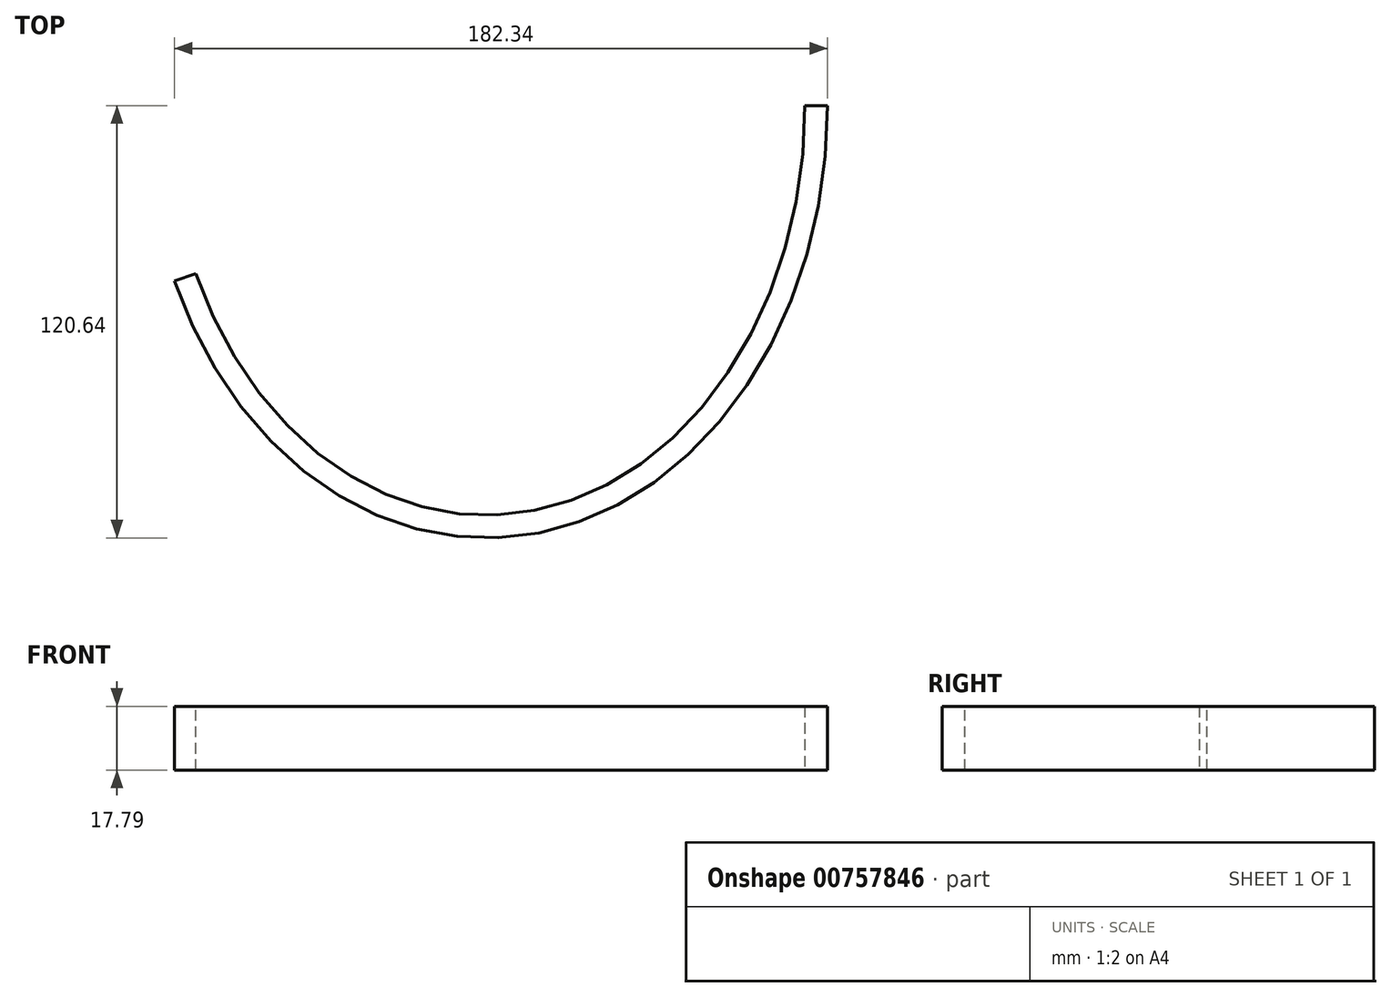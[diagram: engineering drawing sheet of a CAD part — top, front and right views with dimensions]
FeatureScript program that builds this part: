
annotation { "Feature Type Name" : "Feature", "Feature Type Description" : "" }
export const myFeature = defineFeature(function(context is Context, id is Id, definition is map)
    precondition{}
    {
        {
            var Q0;
            Q0=qCreatedBy(makeId("Top.planeOp"),FACE);
            var sketch = newSketch(context, id + "F0", { "sketchPlane" : qUnion([Q0])});
            skEllipse(sketch, "E0", {"center": v(0, 0) * mm, "majorRadius": 114.3 * mm, "minorRadius": 88.9 * mm, "majorAxis": v(0, 1), "construction": true});
            skPoint(sketch, "E1", {"position": v(-81.1, 46.82) * mm});
            skPoint(sketch, "E2", {"position": v(-81.1, -46.82) * mm});
            skLineSegment(sketch, "E3", {"start": v(0, 0) * mm, "end": v(-81.1, 46.82) * mm, "construction": true});
            skLineSegment(sketch, "E4", {"start": v(0, 0) * mm, "end": v(-81.1, -46.82) * mm, "construction": true});
            skLineSegment(sketch, "E5", {"start": v(-88.9, 0) * mm, "end": v(88.9, 0) * mm, "construction": true});
            skSolve(sketch);
        }
        {
            var Q0;
            Q0=qCreatedBy(makeId("Front.planeOp"),FACE);
            var sketch = newSketch(context, id + "F1", { "sketchPlane" : qUnion([Q0])});
            skPoint(sketch, "E6.0", {"position": v(88.9, 0) * mm});
            skLineSegment(sketch, "E7", {"start": v(88.9, 0) * mm, "end": v(88.9, 9.52) * mm});
            skLineSegment(sketch, "E8", {"start": v(88.9, 9.53) * mm, "end": v(95.25, 9.53) * mm});
            skLineSegment(sketch, "E9", {"start": v(95.25, 9.52) * mm, "end": v(95.25, -8.25) * mm});
            skLineSegment(sketch, "E10", {"start": v(95.25, -8.25) * mm, "end": v(88.9, -8.25) * mm});
            skLineSegment(sketch, "E11", {"start": v(88.9, -8.25) * mm, "end": v(88.9, 0) * mm});
            skLineSegment(sketch, "E12", {"start": v(0, 0) * mm, "end": v(0, 49.92) * mm});
            skSolve(sketch);
        }
        {
            var Q0;
            Q0=qCreatedBy(makeId("Top.planeOp"),FACE);
            var sketch = newSketch(context, id + "F2", { "sketchPlane" : qUnion([Q0])});
            skEllipticalArc(sketch, "E13.0", {});
            skPoint(sketch, "E14.0", {"position": v(-81.1, 46.82) * mm});
            skPoint(sketch, "E15.0", {"position": v(-81.1, -46.82) * mm});
            const initialGuessF2  = {"E13.0": [0, 0, 0, 1, 0.1143, 0.0889, 1.992860125578451, 1.1487325280113436]};
            skSetInitialGuess(sketch, initialGuessF2);
            skSolve(sketch);
        }
        {
            var Q0;
            Q0=makeQuery(id+"F1.imprint","IMPRINT",FACE,{"disambiguationData":[TD([[makeQuery(id+"F1.imprint","IMPRINT",EDGE,{"derivedFrom":sQuery(id+"F1.wireOp",EDGE,"E7")}),-1.0]])]});
            var Q1;
            Q1=sQuery(id+"F2.wireOp",EDGE,"E13.0");
            sweep(context, id + "F3", {"profiles" : qUnion([Q0]), "path" : qUnion([Q1])});
        }
        {
            var Q0;
            Q0=qCreatedBy(makeId("Front.planeOp"),FACE);
            var sketch = newSketch(context, id + "F4", { "sketchPlane" : qUnion([Q0])});
            skLineSegment(sketch, "E16.bottom", {"start": v(113.91, 28.04) * mm, "end": v(-113.91, 28.04) * mm});
            skLineSegment(sketch, "E16.top", {"start": v(113.91, -28.04) * mm, "end": v(-113.91, -28.04) * mm});
            skLineSegment(sketch, "E16.left", {"start": v(113.91, 28.04) * mm, "end": v(113.91, -28.04) * mm});
            skLineSegment(sketch, "E16.right", {"start": v(-113.91, 28.04) * mm, "end": v(-113.91, -28.04) * mm});
            skPoint(sketch, "E16.middle", {"position": v(0, 0) * mm});
            skSolve(sketch);
        }
        {
            var Q0;
            Q0=makeQuery(id+"F4.imprint","IMPRINT",FACE,{"disambiguationData":[TD([[makeQuery(id+"F4.imprint","IMPRINT",EDGE,{"derivedFrom":sQuery(id+"F4.wireOp",EDGE,"E16.bottom")}),1.0]])]});
            extrude(context, id + "F5", {"entities" : qUnion([Q0]), "operationType" : NewBodyOperationType.REMOVE, "oppositeDirection" : true, "depth" : 254 * mm, "offsetDistance" : 25.4 * mm});
        }
    });
